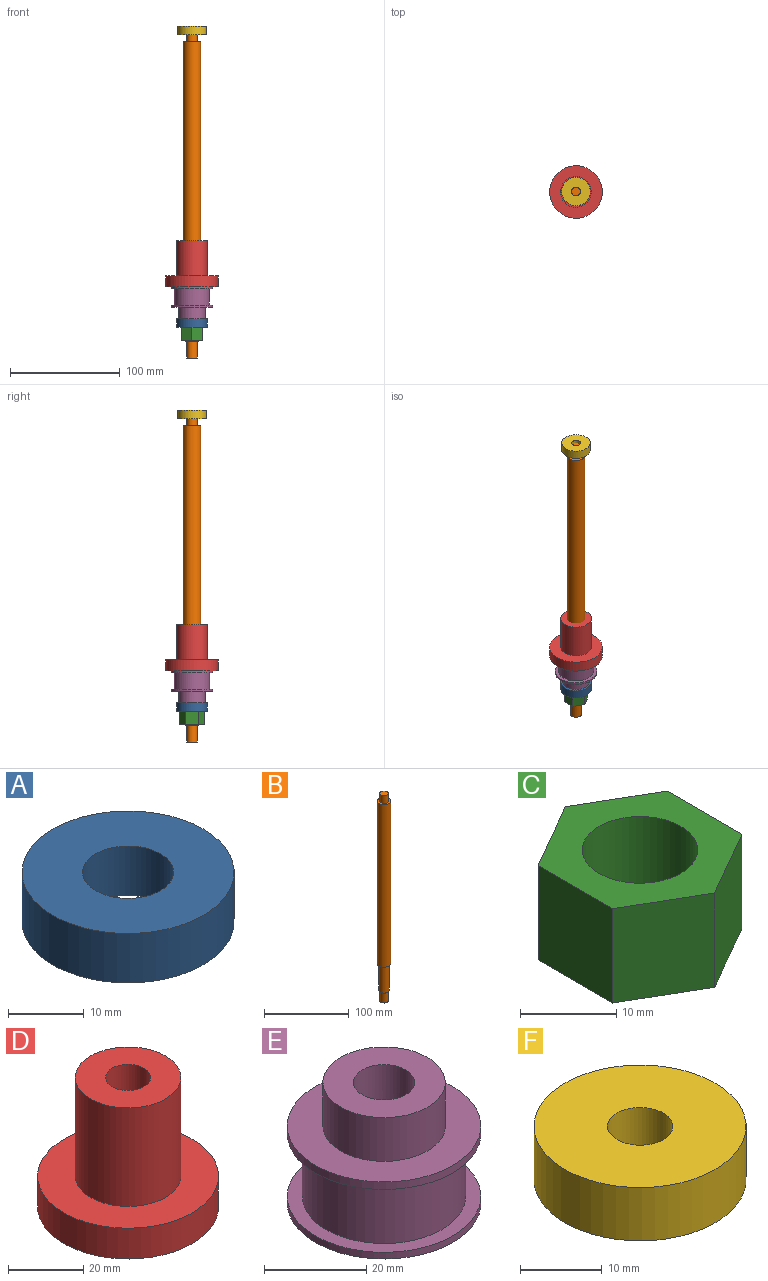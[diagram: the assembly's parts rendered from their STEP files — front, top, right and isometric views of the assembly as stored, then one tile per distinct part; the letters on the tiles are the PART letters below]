
ASSEMBLY  parts=6 mates=5
PART A: 4 faces, bbox 28x28x8 mm
  f0: cylinder r=6mm len=12mm, axis (0,0,-1), area 301.6mm2, adj f2,f3
  f1: cylinder r=14mm len=28mm, axis (0,0,-1), area 703.7mm2, adj f2,f3
  f2: plane 28x28mm, normal (0,0,1), area 502.7mm2, adj f0,f1
  f3: plane 28x28mm, normal (0,0,-1), area 502.7mm2, adj f0,f1
PART B: 9 faces, bbox 16x16x300 mm
  f0: cylinder r=6mm len=39mm, axis (0,0,-1), area 1470.3mm2, adj f1,f5
  f1: plane 12x12mm, normal (0,0,-1), area 34.6mm2, adj f0,f3
  f2: plane 10x10mm, normal (0,0,-1), area 78.5mm2, adj f3
  f3: cylinder r=5mm len=15mm, axis (0,0,-1), area 471.2mm2, adj f1,f2
  f4: cylinder r=8mm len=235mm, axis (0,0,-1), area 11812.4mm2, adj f5,f8
  f5: plane 16x16mm, normal (0,0,-1), area 88mm2, adj f0,f4
  f6: plane 10x10mm, normal (0,0,1), area 78.5mm2, adj f7
  f7: cylinder r=5mm len=11mm, axis (0,0,-1), area 345.6mm2, adj f6,f8
  f8: plane 16x16mm, normal (0,0,1), area 122.5mm2, adj f4,f7
PART C: 9 faces, bbox 19x21.9x12 mm
  f0: plane 12x9.5mm, normal (-0.5,-0.87,0), area 131.6mm2, adj f1,f5,f7,f8
  f1: plane 12x9.5mm, normal (0.5,-0.87,0), area 131.6mm2, adj f0,f2,f7,f8
  f2: plane 12x10.97mm, normal (1,0,0), area 131.6mm2, adj f1,f3,f7,f8
  f3: plane 12x9.5mm, normal (0.5,0.87,0), area 131.6mm2, adj f2,f4,f7,f8
  f4: plane 12x9.5mm, normal (-0.5,0.87,0), area 131.6mm2, adj f3,f5,f7,f8
  f5: plane 12x10.97mm, normal (-1,0,0), area 131.6mm2, adj f0,f4,f7,f8
  f6: cylinder r=6mm len=12mm, axis (0,0,-1), area 452.4mm2, adj f7,f8
  f7: plane 21.94x19mm, normal (0,0,1), area 199.5mm2, adj f0,f1,f2,f3,f4,f5,f6
  f8: plane 21.94x19mm, normal (0,0,-1), area 199.5mm2, adj f0,f1,f2,f3,f4,f5,f6
PART D: 6 faces, bbox 48x48x42 mm
  f0: cylinder r=24mm len=48mm, axis (0,0,-1), area 1508mm2, adj f1,f2
  f1: plane 48x48mm, normal (0,0,1), area 1193.8mm2, adj f0,f3
  f2: plane 48x48mm, normal (0,0,-1), area 1696.5mm2, adj f0,f5
  f3: cylinder r=14mm len=32mm, axis (0,0,-1), area 2814.9mm2, adj f1,f4
  f4: plane 28x28mm, normal (0,0,1), area 502.7mm2, adj f3,f5
  f5: cylinder r=6mm len=42mm, axis (0,0,1), area 1583.4mm2, adj f2,f4
PART E: 10 faces, bbox 38x38x29 mm
  f0: cylinder r=19mm len=38mm, axis (0,0,-1), area 214.9mm2, adj f1,f3
  f1: plane 38x38mm, normal (0,0,1), area 681.7mm2, adj f0,f7
  f2: cylinder r=16mm len=32mm, axis (0,0,-1), area 1518mm2, adj f3,f4
  f3: plane 38x38mm, normal (0,0,-1), area 329.9mm2, adj f0,f2
  f4: plane 38x38mm, normal (0,0,1), area 329.9mm2, adj f2,f6
  f5: plane 38x38mm, normal (0,0,-1), area 1021mm2, adj f6,f9
  f6: cylinder r=19mm len=38mm, axis (0,0,-1), area 191mm2, adj f4,f5
  f7: cylinder r=12mm len=24mm, axis (0,0,-1), area 791.7mm2, adj f1,f8
  f8: plane 24x24mm, normal (0,0,1), area 339.3mm2, adj f7,f9
  f9: cylinder r=6mm len=29mm, axis (0,0,-1), area 1093.3mm2, adj f5,f8
PART F: 4 faces, bbox 26x26x8 mm
  f0: cylinder r=4mm len=8mm, axis (0,0,-1), area 201.1mm2, adj f2,f3
  f1: cylinder r=13mm len=26mm, axis (0,0,-1), area 653.5mm2, adj f2,f3
  f2: plane 26x26mm, normal (0,0,1), area 480.7mm2, adj f0,f1
  f3: plane 26x26mm, normal (0,0,-1), area 480.7mm2, adj f0,f1
PLACE A rot(axis=(0,1,0),0deg) t=(0,0,28)mm
PLACE B at identity
PLACE C rot(axis=(0,1,0),0deg) t=(0,0,16)mm
PLACE D t=(0,0,65)mm
PLACE E rot(axis=(0,1,0),180deg) t=(0,0,65)mm
PLACE F t=(0,0,295)mm
MATE fastened A.f0 <-> E.f9  axis (0,0,1) through (0,0,36)mm
MATE fastened C.f6 <-> A.f0  axis (0,0,1) through (0,0,28)mm
MATE fastened E.f9 <-> B.f0  axis (0,0,1) through (0,0,65)mm
MATE fastened D.f5 <-> B.f4  axis (0,0,-1) through (0,0,65)mm
MATE fastened F.f1 <-> B.f3  axis (0,0,-1) through (0,0,295)mm
